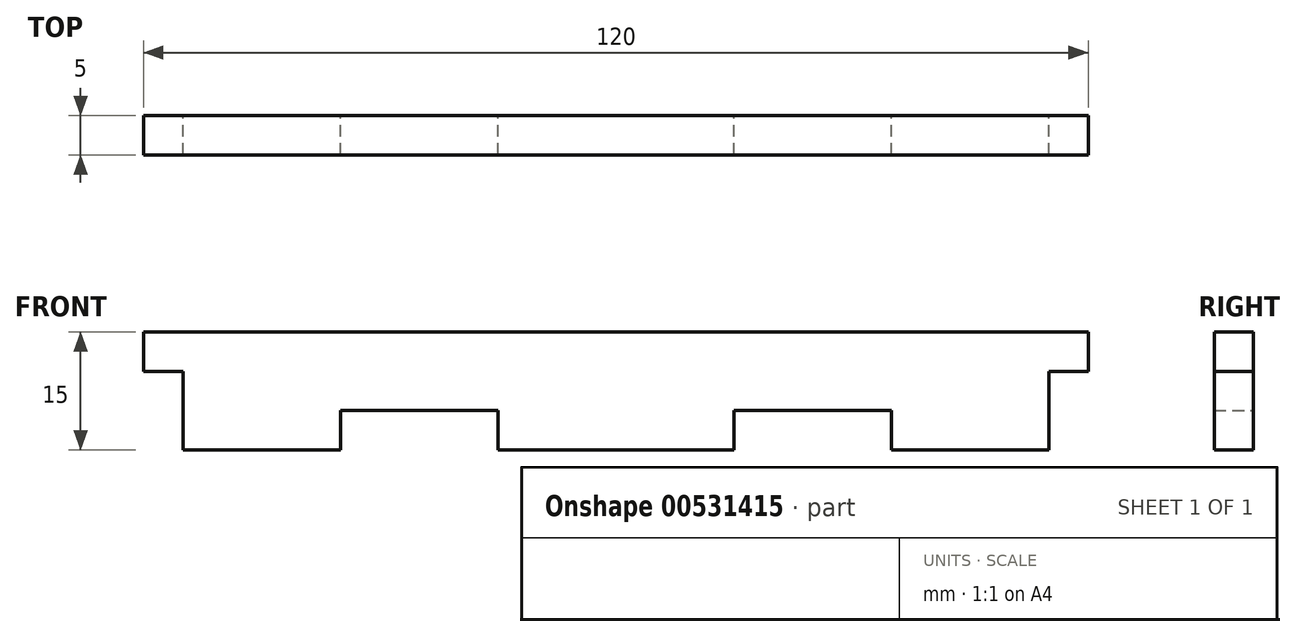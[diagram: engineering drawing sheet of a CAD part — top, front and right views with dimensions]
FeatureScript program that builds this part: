
annotation { "Feature Type Name" : "Feature", "Feature Type Description" : "" }
export const myFeature = defineFeature(function(context is Context, id is Id, definition is map)
    precondition{}
    {
        {
            var Q0;
            Q0=qCreatedBy(makeId("Front.planeOp"),FACE);
            var sketch = newSketch(context, id + "F0", { "sketchPlane" : qUnion([Q0])});
            skLineSegment(sketch, "E0.bottom", {"start": v(55, 5) * mm, "end": v(-55, 5) * mm});
            skLineSegment(sketch, "E0.top", {"start": v(35, -5) * mm, "end": v(15, -5) * mm});
            skLineSegment(sketch, "E0.left", {"start": v(55, 0) * mm, "end": v(55, -5) * mm});
            skLineSegment(sketch, "E0.right", {"start": v(-55, 0) * mm, "end": v(-55, -5) * mm});
            skPoint(sketch, "E0.middle", {"position": v(0, 0) * mm});
            skLineSegment(sketch, "E1", {"start": v(-55, 5) * mm, "end": v(-60, 5) * mm, "construction": true});
            skLineSegment(sketch, "E2", {"start": v(-60, 5) * mm, "end": v(-60, -10) * mm, "construction": true});
            skLineSegment(sketch, "E3", {"start": v(-60, -10) * mm, "end": v(60, -10) * mm, "construction": true});
            skLineSegment(sketch, "E4", {"start": v(60, -10) * mm, "end": v(60, 5) * mm, "construction": true});
            skLineSegment(sketch, "E5", {"start": v(60, 5) * mm, "end": v(55, 5) * mm, "construction": true});
            skLineSegment(sketch, "E6", {"start": v(55, 5) * mm, "end": v(60, 5) * mm});
            skLineSegment(sketch, "E7", {"start": v(60, 0) * mm, "end": v(55, 0) * mm});
            skLineSegment(sketch, "E8", {"start": v(60, 5) * mm, "end": v(60, 0) * mm});
            skLineSegment(sketch, "E9", {"start": v(-55, 5) * mm, "end": v(-60, 5) * mm});
            skLineSegment(sketch, "E10", {"start": v(-60, 0) * mm, "end": v(-55, 0) * mm});
            skLineSegment(sketch, "E11", {"start": v(-60, 5) * mm, "end": v(-60, 0) * mm});
            skLineSegment(sketch, "E12", {"start": v(-55, -5) * mm, "end": v(-55, -10) * mm});
            skLineSegment(sketch, "E13", {"start": v(-55, -10) * mm, "end": v(-35, -10) * mm});
            skLineSegment(sketch, "E14", {"start": v(-35, -10) * mm, "end": v(-35, -5) * mm});
            skLineSegment(sketch, "E15", {"start": v(-35, -5) * mm, "end": v(-15, -5) * mm});
            skLineSegment(sketch, "E16", {"start": v(-15, -5) * mm, "end": v(-15, -10) * mm});
            skLineSegment(sketch, "E17.MirrorCS", {"start": v(15, -5) * mm, "end": v(15, -10) * mm});
            skLineSegment(sketch, "E18.MirrorCS", {"start": v(35, -10) * mm, "end": v(35, -5) * mm});
            skLineSegment(sketch, "E19", {"start": v(-15, -10) * mm, "end": v(15, -10) * mm});
            skLineSegment(sketch, "E20", {"start": v(35, -10) * mm, "end": v(55, -10) * mm});
            skLineSegment(sketch, "E21", {"start": v(55, -10) * mm, "end": v(55, -5) * mm});
            skLineSegment(sketch, "E22.trimOffspring", {"start": v(-15, -5) * mm, "end": v(-35, -5) * mm});
            skSolve(sketch);
        }
        {
            var Q0;
            Q0 = qSketchRegion(id + "F0", true);
            extrude(context, id + "F1", {"entities" : qUnion([Q0]), "depth" : 5 * mm, "offsetDistance" : 25 * mm});
        }
    });
